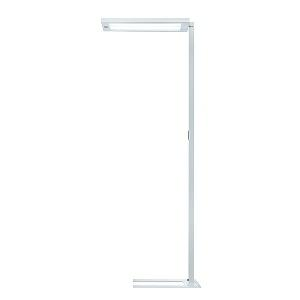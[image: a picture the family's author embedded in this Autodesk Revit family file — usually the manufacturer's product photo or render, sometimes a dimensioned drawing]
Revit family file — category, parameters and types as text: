
# Revit family: lavigo_-_dps_9000_840_r_g2_00803363_38cd
name_source: partatom
category: Lighting Fixtures
units: mm (PartAtom-declared; Revit-internal decimal feet)

## family parameters
Cut with Voids When Loaded = No
Host = Face
Light Source = No
Part Type = Normal
Room Calculation Point = No
Round Connector Dimension = Use Diameter
Shared = No

## types (1)
- LAVIGO - DPS 9000/840/R/G2 (1 x LED, 8950 lm, 4000K)
    Apparent Load = 63 VA
    Approval mark = CE
    CIE Flux Codes = 60 87 97 20 100
    Color Rendering = 80-89
    Color Temperature = 4000K
    Control Gear = Electronic ballast
    Default Elevation = 1800 mm
    Description = DPS 9000/840/R/G2|Free-standing luminaire|light source: LED|work equipment: Electronic ballast|connected load: 220-240 V, 50/60 Hz|Power consumption: approx. 63 W|standby: approx. 0,50|power factor: approx. 0,910|luminous flux: 8950 lm|luminous efficacy: 142 lm/W|light distribution: Direct/indirect|direct ratio: approx. 20 %|colour temperature: Cold white, ca. 4000 K|color rendering index (CRI): >= 80|chromaticity tolerance:  3 SDCM|technology: Presence and daylight sensor control (PIR)|operation: Multi-function switch|luminaire body|material: Steel/plastic|surface: Painted|colour: White|lamp cover: Acrylic (PMMA), Satine|tubular section|material: Steel tube|surface: Painted|Form: Tubular section upright|colour of tubular section: White|luminaire base|Form: C-form flat|weight (net): approx. 19.7 kg|mains lead: 3.00 m Mains plug CEE 7/VII|Fastening: Floor standing base|decorative contrast side parts: Flint grey|glare control: Prism aperture|luminance(L65): <= 3000 cd/m|unified glare rating(4H 8H): <=  16|special features: Luminaire head detachable, Cradle to Cradle Certified TM, Direct light component with edge light and light-guide technology for homogenous light exit, Flicker-free, Integrated light and presence sensor PIR, Retrofittable with TALK module, Separated, direct and indirect light individually adjustable|
    Frequency = 50 Hz
    Height = 36 mm
    Lamp = 1 x LED
    Lamp Light Flux = 8950 lm
    Lamp count = 1
    Length = 675 mm
    Luminous efficacy = 142 lm/W
    Manufacturer = Waldmann
    ModVariant = No
    Model = 00803363
    Mounting Place = Floor
    Mounting Type = Freestanding
    Number of Poles = 1
    OnlyDefault = Yes
    Power Factor = 1
    Product Name = LAVIGO - DPS 9000/840/R/G2
    Product group = Free standing luminaire
    ProductGroupID = 13
    Protection Class = Protection class I
    Protection Degree = IP 20
    RLX_Detail_Level = 1
    RLX_Emergency_Light_Flux = 0 lm
    RLX_Emergency_Type = 0
    RLX_Emergency_Type_DB = No
    RlxData = <blob elided: 37637 chars, md5=880c2ddd>
    Socket = socket
    Standby Power = 0 W
    System Light Flux = 8950 lm
    System Power = 63 W
    Type Comments = Product without accessories
    Type Image = 121695000-00610208.jpg
    URL = http://relux.com
    VarID = ---
    Voltage = 230 V
    Voltage Range = 220-240 V
    Weight = 0.00 kg
    Width = 320 mm

## geometry (parser evidence)
native form markers: Blend x4, Sweep x14
no freeform markers — native parametric forms only
